# Revit family: Toilet-Paper-Holder-American_Standard-TS_Series-7455230
name_source: partatom
category: Specialty Equipment
revit_build: Autodesk Revit 2014 (Build: 20130308_1515(x64)
units: mm (PartAtom-declared; Revit-internal decimal feet)

## types (2) — shared parameters
Assembly Code = C1030220
Default Elevation = 48"
Description = TS Series Bath Accessories Toilet Paper Holder
Finish = Metal-American Standard-002-Polished Chrome
Height = 2 1/4"
Installation Type = Wall Mount
Length = 8 29/32"
Manufacturer = American Standard
Material = Metal-American Standard-002-Polished Chrome
Model = 7455230
Price = Prices may vary. Please consult Manufacturer Representative for most up-to-date price list.
Specification = Toilet Paper Holder shall feature metal construction. Shall feature concealed mounting with no exposed set screws.
URL = https://www.americanstandard-us.com
Warranty Information = One Year General Product Warranty
Width = 3 7/16"

## per-type parameters (varying)
| type | Product Documentation Link | Product Page URL |
| 7455230 | https://www.americanstandard-us.com | https://www.americanstandard-us.com |
| 7455024 |  |  |

## geometry (parser evidence)
native form markers: Sweep x1
no freeform markers — native parametric forms only
